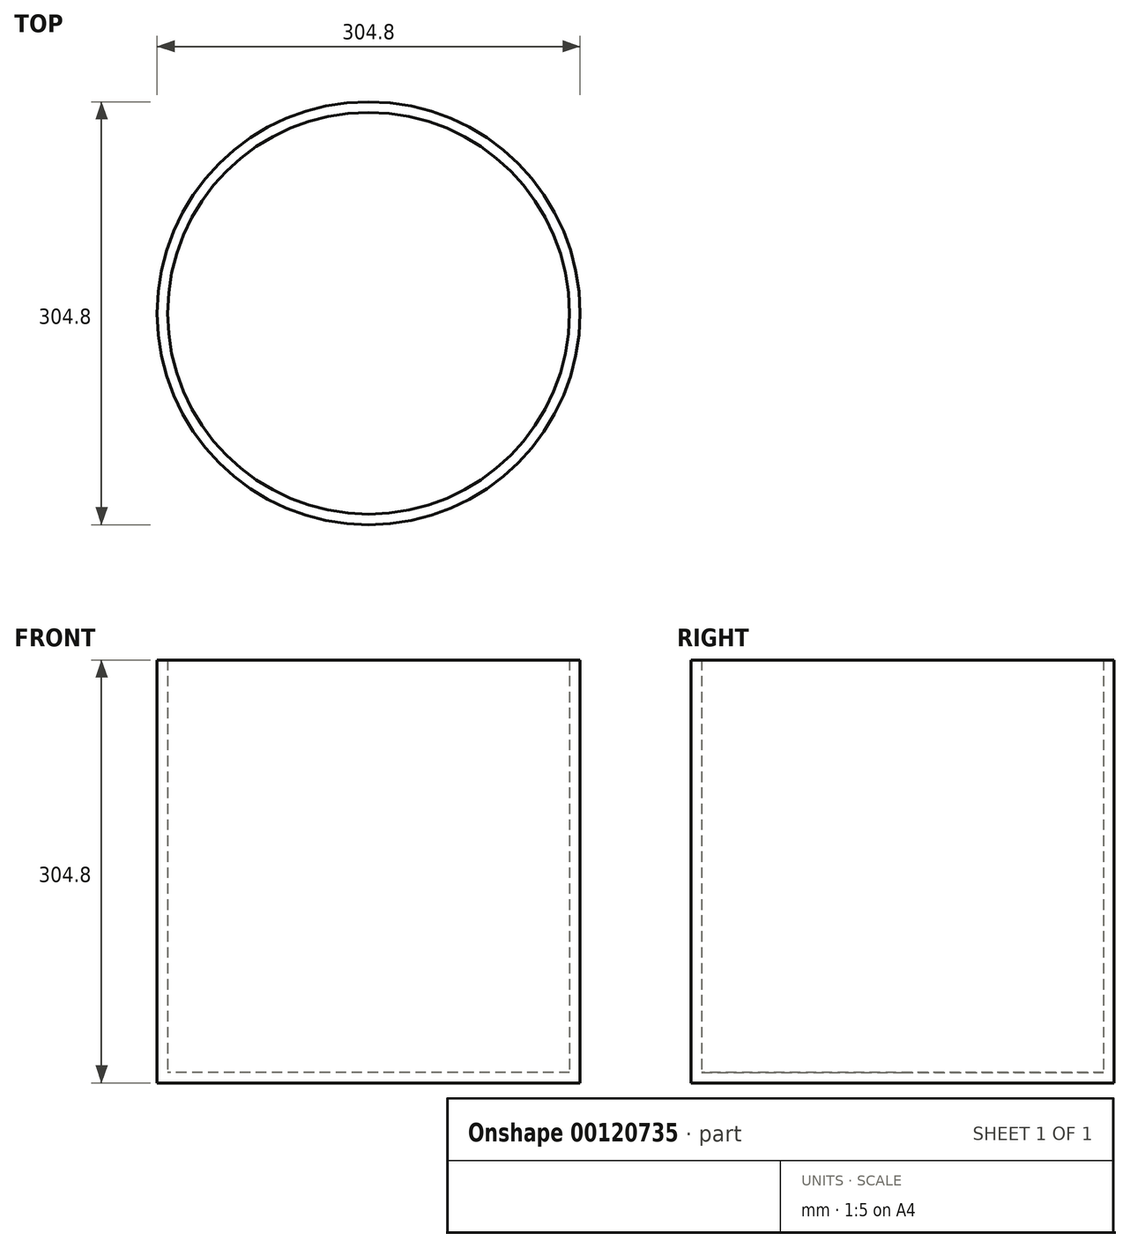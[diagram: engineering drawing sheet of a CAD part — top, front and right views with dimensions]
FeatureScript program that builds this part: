
annotation { "Feature Type Name" : "Feature", "Feature Type Description" : "" }
export const myFeature = defineFeature(function(context is Context, id is Id, definition is map)
    precondition{}
    {
        {
            var Q0;
            Q0=qCreatedBy(makeId("Top.planeOp"),FACE);
            var sketch = newSketch(context, id + "F0", { "sketchPlane" : qUnion([Q0])});
            skCircle(sketch, "E0", {"center": v(0, 0) * mm, "radius": 152.4 * mm});
            skSolve(sketch);
        }
        {
            var Q0;
            Q0=makeQuery(id+"F0.imprint","IMPRINT",FACE,{"disambiguationData":[TD([[makeQuery(id+"F0.imprint","IMPRINT",EDGE,{"derivedFrom":sQuery(id+"F0.wireOp",EDGE,"E0")}),1.0]])]});
            extrude(context, id + "F1", {"entities" : qUnion([Q0]), "endBound" : BoundingType.SYMMETRIC, "depth" : 304.8 * mm});
        }
        {
            var Q0;
            Q0=makeQuery(id+"F1.opExtrude","CAP_FACE",FACE,{"disambiguationData":[OSD([sQuery(id+"F0.wireOp",EDGE,"E0")])],"isStart":false});
            shell(context, id + "F2", {"entities" : qUnion([Q0]), "thickness" : 7.62 * mm});
        }
    });
